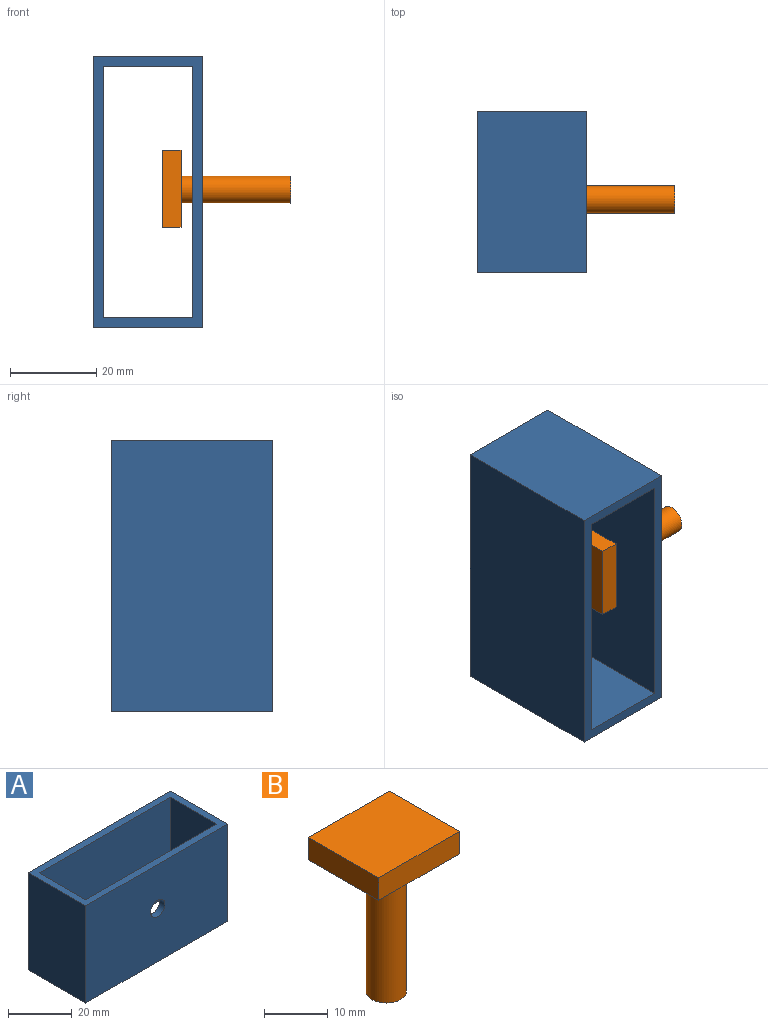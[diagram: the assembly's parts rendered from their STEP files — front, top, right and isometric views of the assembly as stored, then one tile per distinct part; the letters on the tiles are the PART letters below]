
ASSEMBLY  parts=2 mates=1
PART A: 11 faces, bbox 62.8x25.4x37.3 mm
  f0: plane 62.77x25.4mm, normal (0,0,-1), area 392.4mm2, adj f2,f3,f4,f5,f6,f7,f8,f9
  f1: plane 62.77x25.4mm, normal (0,0,1), area 392.4mm2, adj f2,f3,f4,f5,f6,f7,f8,f9
  f2: plane 37.31x25.4mm, normal (-1,0,0), area 947.8mm2, adj f0,f1,f4,f5
  f3: plane 37.31x25.4mm, normal (1,0,0), area 947.8mm2, adj f0,f1,f4,f5
  f4: plane 62.77x37.31mm, normal (0,-1,0), area 2310.6mm2, adj f0,f1,f2,f3,f10
  f5: plane 62.77x37.31mm, normal (0,1,0), area 2342.2mm2, adj f0,f1,f2,f3
  f6: plane 58.19x37.31mm, normal (0,1,0), area 2139.6mm2, adj f0,f1,f7,f9,f10
  f7: plane 37.31x20.66mm, normal (1,0,0), area 770.8mm2, adj f0,f1,f6,f8
  f8: plane 58.19x37.31mm, normal (0,-1,0), area 2171.3mm2, adj f0,f1,f7,f9
  f9: plane 37.31x20.66mm, normal (-1,0,0), area 770.8mm2, adj f0,f1,f6,f8
  f10: cylinder r=3.17mm len=6.35mm, axis (0,-1,0), area 46.7mm2, adj f4,f6
PART B: 8 faces, bbox 17.9x15.6x29.7 mm
  f0: cylinder r=3.17mm len=25.4mm, axis (0,0,-1), area 506.7mm2, adj f1,f7
  f1: plane 6.35x6.35mm, normal (0,0,-1), area 31.7mm2, adj f0
  f2: plane 17.9x4.32mm, normal (0,-1,0), area 77.3mm2, adj f3,f5,f6,f7
  f3: plane 15.56x4.32mm, normal (1,0,0), area 67.2mm2, adj f2,f4,f6,f7
  f4: plane 17.9x4.32mm, normal (0,1,0), area 77.3mm2, adj f3,f5,f6,f7
  f5: plane 15.56x4.32mm, normal (-1,0,0), area 67.2mm2, adj f2,f4,f6,f7
  f6: plane 17.9x15.56mm, normal (0,0,1), area 278.5mm2, adj f2,f3,f4,f5
  f7: plane 17.9x15.56mm, normal (0,0,-1), area 246.9mm2, adj f0,f2,f3,f4,f5
PLACE A rot(axis=(0.58,-0.58,0.58),120deg) t=(-27.94,19.42,-34.15)mm fixed
PLACE B rot(axis=(0,-1,0),90deg) t=(17.78,-0.97,-2.24)mm
MATE slider A.f10 <-> B.f0  axis (1,0,0) through (-2.54,-0.97,-2.24)mm
